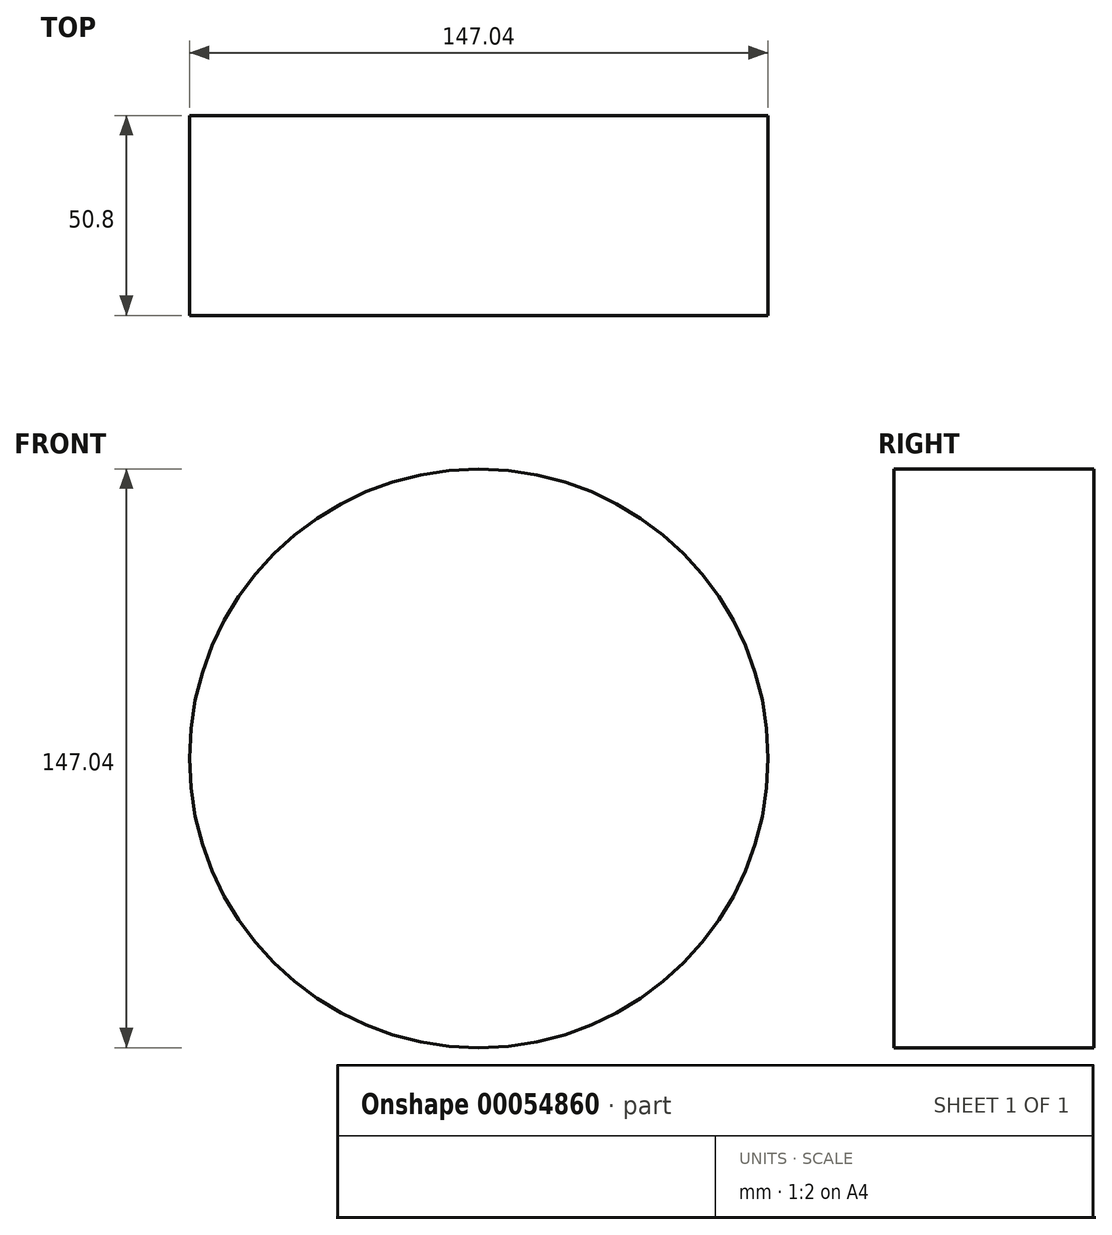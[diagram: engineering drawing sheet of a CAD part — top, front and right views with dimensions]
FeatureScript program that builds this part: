
annotation { "Feature Type Name" : "Feature", "Feature Type Description" : "" }
export const myFeature = defineFeature(function(context is Context, id is Id, definition is map)
    precondition{}
    {
        {
            var Q0;
            Q0=qCreatedBy(makeId("Front.planeOp"),FACE);
            var sketch = newSketch(context, id + "F0", { "sketchPlane" : qUnion([Q0])});
            skCircle(sketch, "E0", {"center": v(0, 0) * mm, "radius": 73.52 * mm});
            skSolve(sketch);
        }
        {
            var Q0;
            Q0 = qSketchRegion(id + "F0", true);
            extrude(context, id + "F1", {"entities" : qUnion([Q0]), "depth" : 50.8 * mm});
        }
    });
